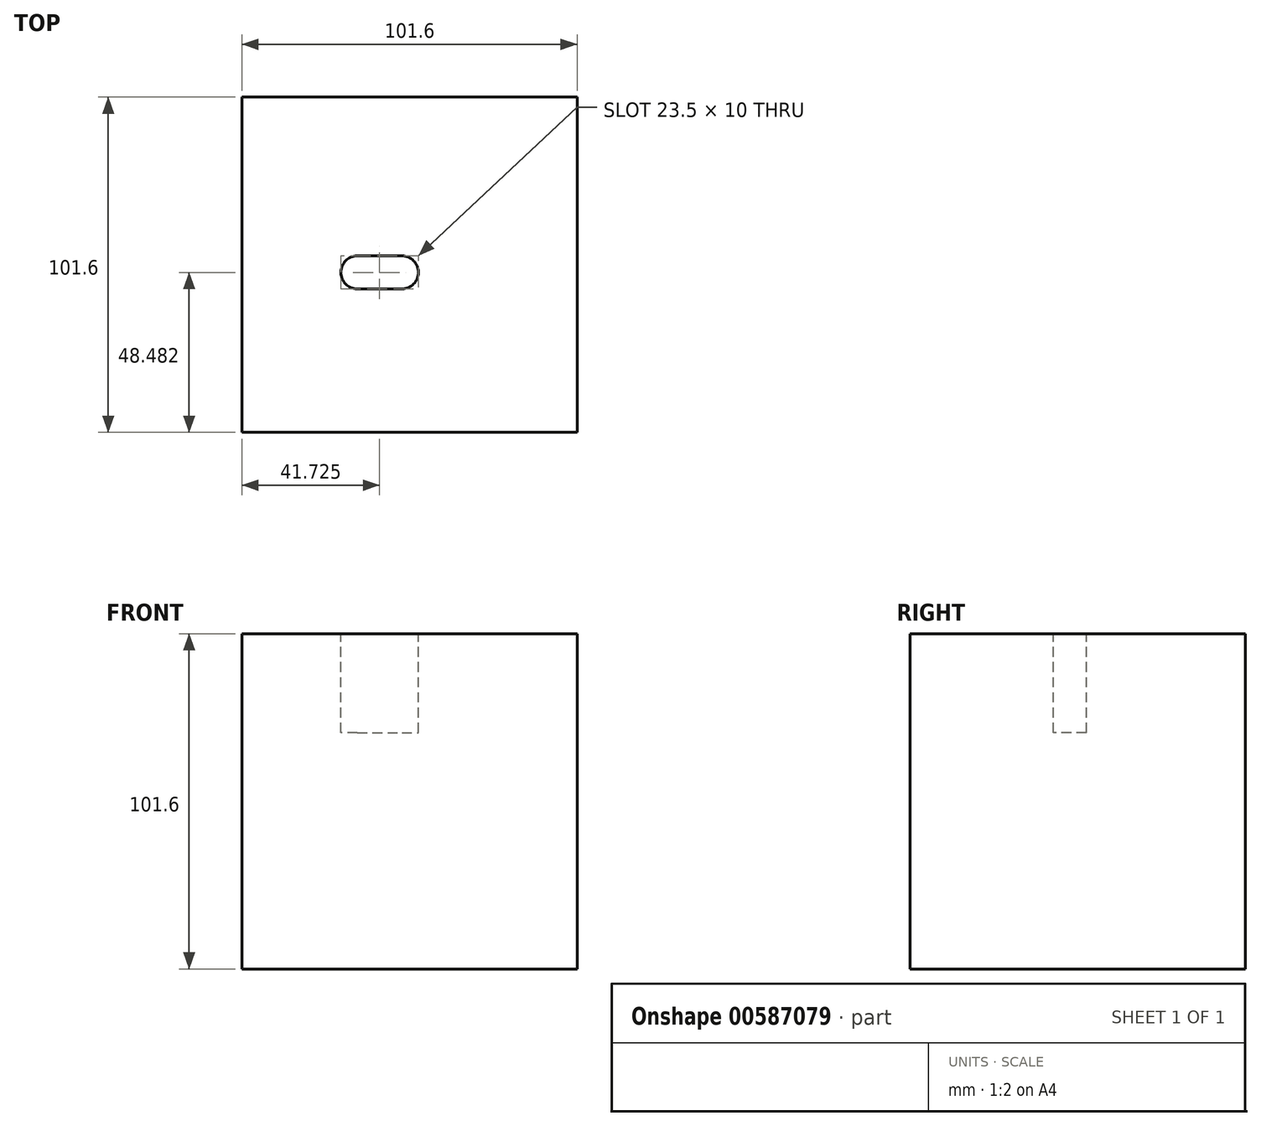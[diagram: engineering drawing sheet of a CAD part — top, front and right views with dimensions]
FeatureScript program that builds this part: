
annotation { "Feature Type Name" : "Feature", "Feature Type Description" : "" }
export const myFeature = defineFeature(function(context is Context, id is Id, definition is map)
    precondition{}
    {
        {
            var Q0;
            Q0=qCreatedBy(makeId("Top.planeOp"),FACE);
            var sketch = newSketch(context, id + "F0", { "sketchPlane" : qUnion([Q0])});
            skLineSegment(sketch, "E0.bottom", {"start": v(50.8, -50.8) * mm, "end": v(-50.8, -50.8) * mm});
            skLineSegment(sketch, "E0.top", {"start": v(50.8, 50.8) * mm, "end": v(-50.8, 50.8) * mm});
            skLineSegment(sketch, "E0.left", {"start": v(50.8, -50.8) * mm, "end": v(50.8, 50.8) * mm});
            skLineSegment(sketch, "E0.right", {"start": v(-50.8, -50.8) * mm, "end": v(-50.8, 50.8) * mm});
            skPoint(sketch, "E0.middle", {"position": v(0, 0) * mm});
            skSolve(sketch);
        }
        {
            var Q0;
            Q0=makeQuery(id+"F0.imprint","IMPRINT",FACE,{"disambiguationData":[TD([[makeQuery(id+"F0.imprint","IMPRINT",EDGE,{"derivedFrom":sQuery(id+"F0.wireOp",EDGE,"E0.bottom")}),-1.0]])]});
            extrude(context, id + "F1", {"entities" : qUnion([Q0]), "depth" : 101.6 * mm, "offsetDistance" : 25.4 * mm});
        }
        {
            var Q0;
            Q0=makeQuery(id+"F1.opExtrude","CAP_FACE",FACE,{"disambiguationData":[OSD([sQuery(id+"F0.wireOp",EDGE,"E0.bottom"),sQuery(id+"F0.wireOp",EDGE,"E0.top"),sQuery(id+"F0.wireOp",EDGE,"E0.left"),sQuery(id+"F0.wireOp",EDGE,"E0.right")])],"isStart":false});
            var sketch = newSketch(context, id + "F2", { "sketchPlane" : qUnion([Q0])});
            skCircle(sketch, "E1", {"center": v(-15.82, -2.32) * mm, "radius": 5 * mm});
            skCircle(sketch, "E2", {"center": v(-2.32, -2.32) * mm, "radius": 5 * mm});
            skLineSegment(sketch, "E3", {"start": v(-15.82, 2.68) * mm, "end": v(-2.32, 2.68) * mm});
            skLineSegment(sketch, "E4", {"start": v(-15.82, -7.32) * mm, "end": v(-2.32, -7.32) * mm});
            skLineSegment(sketch, "E5", {"start": v(-20.82, -2.32) * mm, "end": v(2.68, -2.32) * mm, "construction": true});
            skPoint(sketch, "E6", {"position": v(-20.82, -2.32) * mm});
            skPoint(sketch, "E7", {"position": v(2.68, -2.32) * mm});
            skSolve(sketch);
        }
        {
            var Q0;
            {var subQ0=sQuery(id+"F2.wireOp",EDGE,"E1");var subQ1=makeQuery(id+"F2.imprint","INTERSECT",VERTEX,{"derivedFrom":[subQ0,sQuery(id+"F2.wireOp",EDGE,"E3")]});Q0=makeQuery(id+"F2.imprint","IMPRINT",FACE,{"disambiguationData":[TD([[makeQuery(id+"F2.imprint","IMPRINT",EDGE,{"disambiguationData":[TD([[subQ1,-1.0]])],"derivedFrom":subQ0}),1.0]])]});}
            var Q1;
            {var subQ0=sQuery(id+"F2.wireOp",EDGE,"E3");Q1=makeQuery(id+"F2.imprint","IMPRINT",FACE,{"disambiguationData":[TD([[makeQuery(id+"F2.imprint","IMPRINT",EDGE,{"derivedFrom":subQ0}),-1.0]])]});}
            var Q2;
            {var subQ0=sQuery(id+"F2.wireOp",EDGE,"E2");var subQ1=makeQuery(id+"F2.imprint","INTERSECT",VERTEX,{"derivedFrom":[subQ0,sQuery(id+"F2.wireOp",EDGE,"E3")]});Q2=makeQuery(id+"F2.imprint","IMPRINT",FACE,{"disambiguationData":[TD([[makeQuery(id+"F2.imprint","IMPRINT",EDGE,{"disambiguationData":[TD([[subQ1,-1.0]])],"derivedFrom":subQ0}),1.0]])]});}
            extrude(context, id + "F3", {"entities" : qUnion([Q0, Q1, Q2]), "operationType" : NewBodyOperationType.REMOVE, "oppositeDirection" : true, "depth" : 30 * mm, "offsetDistance" : 25.4 * mm});
        }
    });
